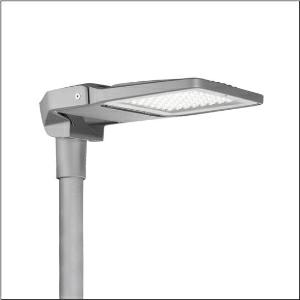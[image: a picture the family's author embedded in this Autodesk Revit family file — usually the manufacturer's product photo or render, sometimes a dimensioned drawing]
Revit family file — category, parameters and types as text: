
# Revit family: floodlight_fl_20_mini___pl43_5xa7672c2a4ac_ff07
name_source: partatom
category: Lighting Fixtures
units: mm (PartAtom-declared; Revit-internal decimal feet)

## family parameters
Cut with Voids When Loaded = No
Host = Face
Light Source = No
Part Type = Normal
Room Calculation Point = No
Round Connector Dimension = Use Diameter
Shared = No

## types (1)
- --- (1 x LED 4000K / CRI = 70 (unbekannt), 13030 lm, 4000K)
    Apparent Load = 96 VA
    CIE Flux Codes = 32 74 99 100 100
    Color Rendering = 70
    Color Temperature = 4000K
    Default Elevation = 1800 mm
    Description = Floodlight FL 20 mini, floodlight, primary light control with lens, of plastic, primary optical cover: protective disc, of toughened safety glass, transparent, light distribution: PL43, light emission: direct distribution, primary light characteristic: asymmetric, installation type: side-entry, post-top, LED, High Power LED, rated luminous flux: 13.030lm, luminous efficacy: 136lm/W, light colour: 740, colour temperature: 4000K, control gear: ECG Plus, control: flexible luminous flux parameterisation, time-dependent luminous flux control, digital communication interface, overheat protection, power reduction, electronic power reduction, with terminal, 5-pole, max. 2.5mm², mains connection: 220..240V, AC, 50/60Hz, rated input power: 96W, LED unit, of diecast aluminium, powder-coated, Siteco® metallic grey (DB 702S), corrosivity category C5 mid according to DIN EN ISO 12944, incl. 1x M20 cable gland for cable Ø 6.5..12mm, inclination adjustable: 0°, 5°, 10°, 15°, please order mast flange separately, length: 565mm, width: 335mm, height: 119mm, housing frame, of diecast aluminium, powder-coated, Siteco® metallic grey (DB 702S), mast flange adapter, of diecast aluminium, powder-coated, Siteco® metallic grey (DB 702S), DALI, protection rating (complete): IP66, insulation class (complete): insulation class II (safety insulation), certification: CE, ENEC, VDE, protection symbol: D, permissible operating ambient temperature: -40..+40°C, permissible operating ambient temperature for outdoor applications: -40..+50°C, standard: DIN EN 12944, packaging unit: 1 piece

Light Distribution: PL43
    Height = 62 mm  [stored 0.203412 ft]
    Lamp = 1 x LED 4000K / CRI >= 70 (unbekannt)
    Lamp Light Flux = 13030 lm
    Lamp count = 1
    Length = 565 mm
    Luminous efficacy = 136 lm/W
    Manufacturer = Siteco
    ModVariant = No
    Model = 5XA7672C2A4AC
    Number of Poles = 1
    OnlyDefault = Yes
    Power Factor = 1
    Product Name = Floodlight FL 20 mini | PL43
    Product group = floodlight | pylon top
    ProductGroupID = 6101
    Protection Class = Protection class II
    Protection Degree = IP 66
    RLX_Detail_Level = 1
    RLX_Emergency_Light_Flux = 0 lm
    RLX_Emergency_Type = 0
    RLX_Emergency_Type_DB = No
    RlxData = <blob elided: 101817 chars, md5=a221173c>
    Socket = socket
    Standby Power = 0 W
    System Light Flux = 13030 lm
    System Power = 96 W
    Type Comments = factory setting: luminous flux: 100 % | dim-lin: 254 | 500 mA
    Type Image = l_1005946.jpg
    URL = http://relux.com
    VarID = @adj_164033
    Voltage = 0 V
    Weight = 0.00 kg
    Width = 335 mm

note: [stored X ft] marks values corroborated as IEEE doubles in the binary element streams (Revit-internal decimal feet)

## geometry (parser evidence)
native form markers: Blend x4, Sweep x15
no freeform markers — native parametric forms only
